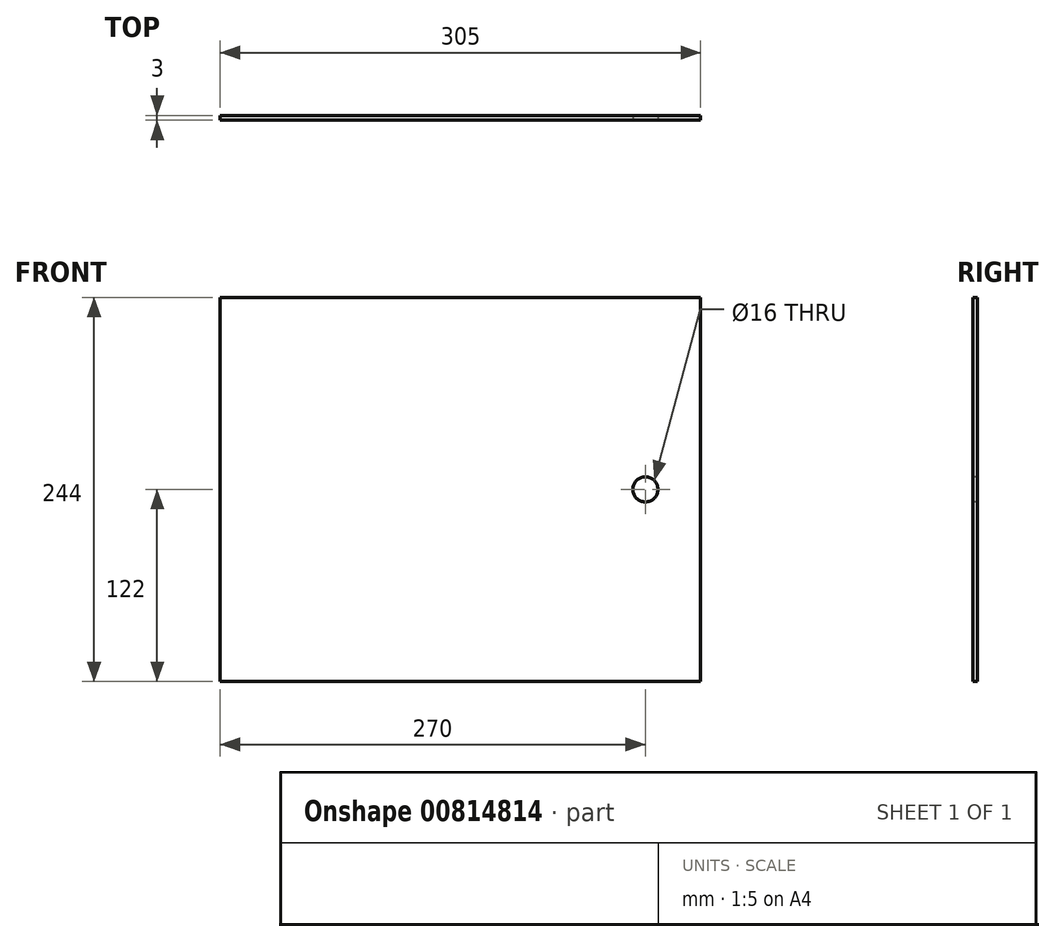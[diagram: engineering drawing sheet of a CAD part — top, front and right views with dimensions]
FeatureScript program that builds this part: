
annotation { "Feature Type Name" : "Feature", "Feature Type Description" : "" }
export const myFeature = defineFeature(function(context is Context, id is Id, definition is map)
    precondition{}
    {
        {
            var Q0;
            Q0=qCreatedBy(makeId("Front.planeOp"),FACE);
            var sketch = newSketch(context, id + "F0", { "sketchPlane" : qUnion([Q0])});
            skLineSegment(sketch, "E0.bottom", {"start": v(-305, 244) * mm, "end": v(0, 244) * mm});
            skLineSegment(sketch, "E0.top", {"start": v(-305, 0) * mm, "end": v(0, 0) * mm});
            skLineSegment(sketch, "E0.left", {"start": v(-305, 244) * mm, "end": v(-305, 0) * mm});
            skLineSegment(sketch, "E0.right", {"start": v(0, 244) * mm, "end": v(0, 0) * mm});
            skSolve(sketch);
        }
        {
            var Q0;
            Q0=makeQuery(id+"F0.imprint","IMPRINT",FACE,{"disambiguationData":[TD([[makeQuery(id+"F0.imprint","IMPRINT",EDGE,{"derivedFrom":sQuery(id+"F0.wireOp",EDGE,"E0.bottom")}),-1.0]])]});
            extrude(context, id + "F1", {"entities" : qUnion([Q0]), "depth" : 3 * mm, "offsetDistance" : 25 * mm});
        }
        {
            var Q0;
            Q0=makeQuery(id+"F1.opExtrude","CAP_FACE",FACE,{"disambiguationData":[OSD([sQuery(id+"F0.wireOp",EDGE,"E0.bottom"),sQuery(id+"F0.wireOp",EDGE,"E0.top"),sQuery(id+"F0.wireOp",EDGE,"E0.left"),sQuery(id+"F0.wireOp",EDGE,"E0.right")])],"isStart":false});
            var sketch = newSketch(context, id + "F2", { "sketchPlane" : qUnion([Q0])});
            skLineSegment(sketch, "E1", {"start": v(0, 122) * mm, "end": v(-35, 122) * mm});
            skSolve(sketch);
        }
        {
            var Q0;
            Q0=sQuery(id+"F2.wireOp",VERTEX,"E1.end");
            var Q1;
            Q1=makeQuery(id+"F1.opExtrude","SWEPT_BODY",BODY,{"disambiguationData":[OSD([sQuery(id+"F0.wireOp",EDGE,"E0.bottom"),sQuery(id+"F0.wireOp",EDGE,"E0.top"),sQuery(id+"F0.wireOp",EDGE,"E0.left"),sQuery(id+"F0.wireOp",EDGE,"E0.right")])]});
            hole(context, id + "F3", {"style" : HoleStyle.SIMPLE, "endStyle" : HoleEndStyle.THROUGH, "holeDiameter" : 16 * mm, "majorDiameter" : 5 * mm, "isTappedThrough" : true, "tappedDepth" : 12 * mm, "tapClearance" : 3, "locations" : qUnion([Q0]), "scope" : qUnion([Q1])});
        }
    });
